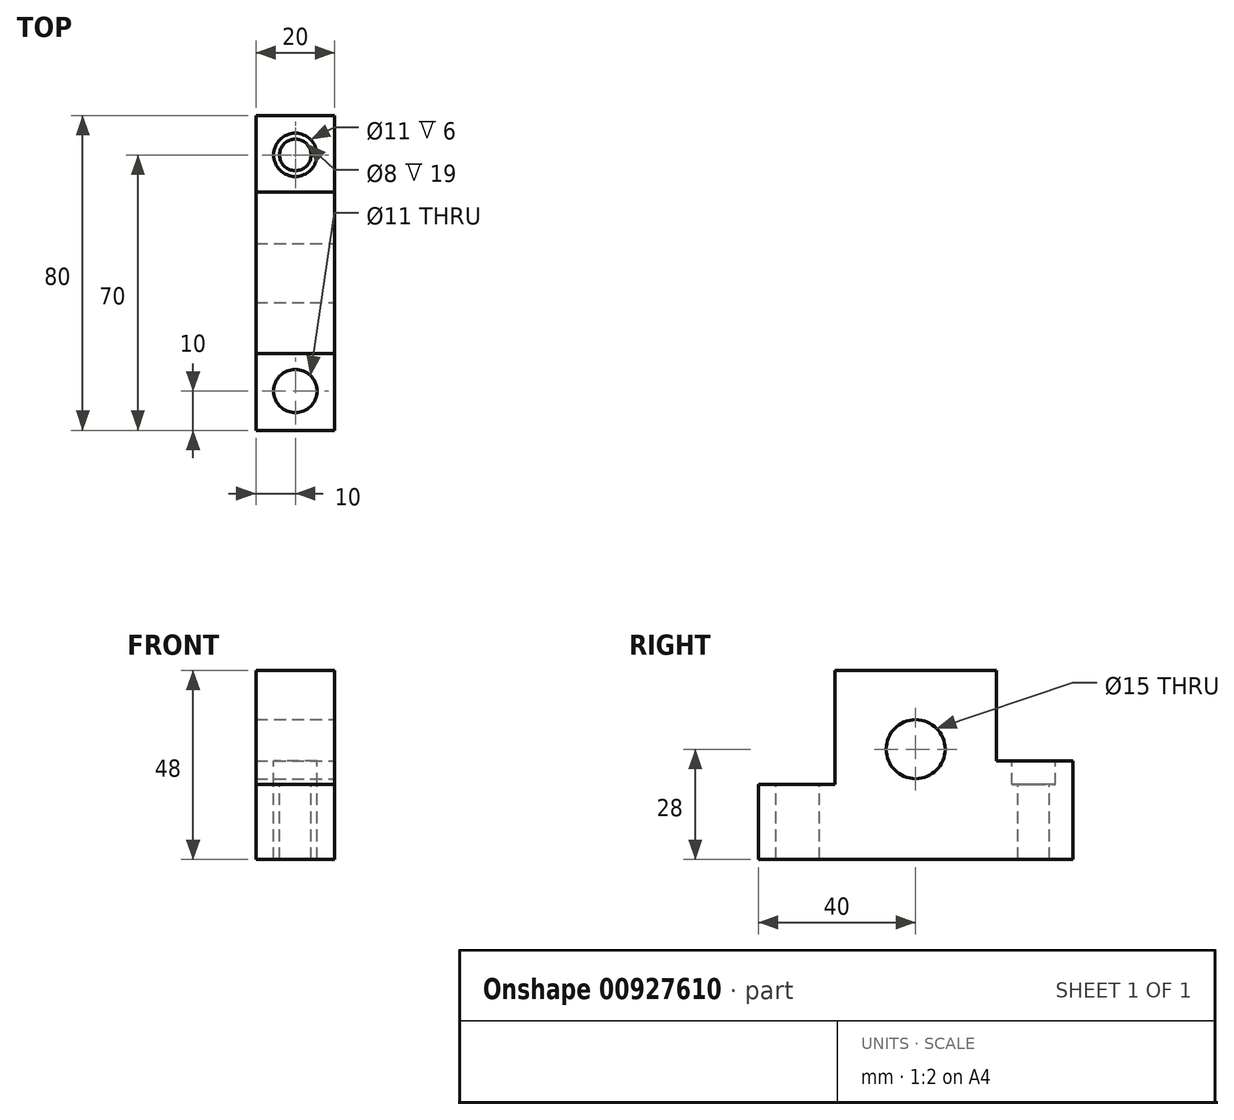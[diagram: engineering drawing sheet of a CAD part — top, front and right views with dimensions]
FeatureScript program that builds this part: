
annotation { "Feature Type Name" : "Feature", "Feature Type Description" : "" }
export const myFeature = defineFeature(function(context is Context, id is Id, definition is map)
    precondition{}
    {
        {
            var Q0;
            Q0=qCreatedBy(makeId("Right.planeOp"),FACE);
            var sketch = newSketch(context, id + "F0", { "sketchPlane" : qUnion([Q0])});
            skLineSegment(sketch, "E0.bottom", {"start": v(40, 24) * mm, "end": v(-40, 24) * mm});
            skLineSegment(sketch, "E0.top", {"start": v(40, -24) * mm, "end": v(-40, -24) * mm});
            skLineSegment(sketch, "E0.left", {"start": v(40, 24) * mm, "end": v(40, -24) * mm});
            skLineSegment(sketch, "E0.right", {"start": v(-40, 24) * mm, "end": v(-40, -24) * mm});
            skPoint(sketch, "E0.middle", {"position": v(0, 0) * mm});
            skSolve(sketch);
        }
        {
            var Q0;
            Q0 = qSketchRegion(id + "F0", true);
            extrude(context, id + "F1", {"entities" : qUnion([Q0]), "depth" : 20 * mm, "offsetDistance" : 25 * mm});
        }
        {
            var Q0;
            Q0=makeQuery(id+"F1.opExtrude","CAP_FACE",FACE,{"disambiguationData":[OSD([sQuery(id+"F0.wireOp",EDGE,"E0.bottom"),sQuery(id+"F0.wireOp",EDGE,"E0.top"),sQuery(id+"F0.wireOp",EDGE,"E0.left"),sQuery(id+"F0.wireOp",EDGE,"E0.right")])],"isStart":false});
            var sketch = newSketch(context, id + "F2", { "sketchPlane" : qUnion([Q0])});
            skLineSegment(sketch, "E1", {"start": v(-74.26, 4) * mm, "end": v(75.01, 4) * mm, "construction": true});
            skCircle(sketch, "E2", {"center": v(0, 4) * mm, "radius": 7.5 * mm});
            skSolve(sketch);
        }
        {
            var Q0;
            Q0=makeQuery(id+"F2.imprint","IMPRINT",FACE,{"disambiguationData":[TD([[makeQuery(id+"F2.imprint","IMPRINT",EDGE,{"derivedFrom":sQuery(id+"F2.wireOp",EDGE,"E2")}),1.0]])]});
            extrude(context, id + "F3", {"entities" : qUnion([Q0]), "operationType" : NewBodyOperationType.REMOVE, "endBound" : BoundingType.THROUGH_ALL, "oppositeDirection" : true, "depth" : 25 * mm, "offsetDistance" : 25 * mm});
        }
        {
            var Q0;
            Q0=makeQuery(id+"F1.opExtrude","CAP_FACE",FACE,{"disambiguationData":[OSD([sQuery(id+"F0.wireOp",EDGE,"E0.bottom"),sQuery(id+"F0.wireOp",EDGE,"E0.top"),sQuery(id+"F0.wireOp",EDGE,"E0.left"),sQuery(id+"F0.wireOp",EDGE,"E0.right")])],"isStart":false});
            var sketch = newSketch(context, id + "F4", { "sketchPlane" : qUnion([Q0])});
            skLineSegment(sketch, "E3", {"start": v(20.5, 56.94) * mm, "end": v(20.5, 1) * mm});
            skLineSegment(sketch, "E4", {"start": v(20.5, 1) * mm, "end": v(58.1, 1) * mm});
            skLineSegment(sketch, "E5.MirrorCS", {"start": v(-20.5, 56.94) * mm, "end": v(-20.5, 1) * mm});
            skLineSegment(sketch, "E6.MirrorCS", {"start": v(-20.5, 1) * mm, "end": v(-58.1, 1) * mm});
            skSolve(sketch);
        }
        {
            var Q0;
            {var subQ0=sQuery(id+"F4.wireOp",EDGE,"E6.MirrorCS");var subQ1=sQuery(id+"F4.wireOp",EDGE,"E5.MirrorCS");var subQ2=makeQuery(id+"F4.imprint","INTERSECT",VERTEX,{"derivedFrom":[subQ1,subQ0]});Q0=makeQuery(id+"F4.imprint","IMPRINT",FACE,{"disambiguationData":[TD([[makeQuery(id+"F4.imprint","IMPRINT",EDGE,{"disambiguationData":[TD([[subQ2,1.0]])],"derivedFrom":subQ1}),-1.0]])]});}
            var Q1;
            {var subQ0=sQuery(id+"F4.wireOp",EDGE,"E4");var subQ1=sQuery(id+"F4.wireOp",EDGE,"E3");var subQ2=makeQuery(id+"F4.imprint","INTERSECT",VERTEX,{"derivedFrom":[subQ1,subQ0]});Q1=makeQuery(id+"F4.imprint","IMPRINT",FACE,{"disambiguationData":[TD([[makeQuery(id+"F4.imprint","IMPRINT",EDGE,{"disambiguationData":[TD([[subQ2,1.0]])],"derivedFrom":subQ1}),1.0]])]});}
            extrude(context, id + "F5", {"entities" : qUnion([Q0, Q1]), "operationType" : NewBodyOperationType.REMOVE, "endBound" : BoundingType.THROUGH_ALL, "oppositeDirection" : true, "depth" : 25 * mm, "offsetDistance" : 25 * mm});
        }
        {
            var Q0;
            Q0=makeQuery(id+"F5.boolean.opBoolean","COPY",FACE,{"derivedFrom":makeQuery(id+"F5.opExtrude","SWEPT_FACE",FACE,{"disambiguationData":[OSD([sQuery(id+"F4.wireOp",EDGE,"E6.MirrorCS")])]})});
            var sketch = newSketch(context, id + "F6", { "sketchPlane" : qUnion([Q0])});
            skLineSegment(sketch, "E7", {"start": v(10, 66.63) * mm, "end": v(10, -85.18) * mm, "construction": true});
            skCircle(sketch, "E8", {"center": v(10, 30) * mm, "radius": 5.5 * mm});
            skCircle(sketch, "E9.MirrorC", {"center": v(10, -30) * mm, "radius": 5.5 * mm});
            skCircle(sketch, "E10", {"center": v(10, 30) * mm, "radius": 4 * mm});
            skCircle(sketch, "E11.MirrorC", {"center": v(10, -30) * mm, "radius": 4 * mm});
            skSolve(sketch);
        }
        {
            var Q0;
            Q0=makeQuery(id+"F6.imprint","IMPRINT",FACE,{"disambiguationData":[TD([[makeQuery(id+"F6.imprint","IMPRINT",EDGE,{"derivedFrom":sQuery(id+"F6.wireOp",EDGE,"E8")}),1.0]])]});
            var Q1;
            Q1=makeQuery(id+"F6.imprint","IMPRINT",FACE,{"disambiguationData":[TD([[makeQuery(id+"F6.imprint","IMPRINT",EDGE,{"derivedFrom":sQuery(id+"F6.wireOp",EDGE,"E9.MirrorC")}),-1.0]])]});
            extrude(context, id + "F7", {"entities" : qUnion([Q0, Q1]), "operationType" : NewBodyOperationType.REMOVE, "oppositeDirection" : true, "depth" : 6 * mm, "offsetDistance" : 25 * mm});
        }
        {
            var Q0;
            Q0=makeQuery(id+"F7.boolean.opBoolean","SPLIT",FACE,{"disambiguationData":[TD([makeQuery(id+"F7.opExtrude","SWEPT_FACE",FACE,{"disambiguationData":[OSD([sQuery(id+"F6.wireOp",EDGE,"E10")])]})])],"derivedFrom":makeQuery(id+"F5.boolean.opBoolean","COPY",FACE,{"derivedFrom":makeQuery(id+"F5.opExtrude","SWEPT_FACE",FACE,{"disambiguationData":[OSD([sQuery(id+"F4.wireOp",EDGE,"E4")])]})})});
            var Q1;
            Q1=makeQuery(id+"F7.boolean.opBoolean","SPLIT",FACE,{"disambiguationData":[TD([makeQuery(id+"F7.opExtrude","SWEPT_FACE",FACE,{"disambiguationData":[OSD([sQuery(id+"F6.wireOp",EDGE,"E11.MirrorC")])]})])],"derivedFrom":makeQuery(id+"F5.boolean.opBoolean","COPY",FACE,{"derivedFrom":makeQuery(id+"F5.opExtrude","SWEPT_FACE",FACE,{"disambiguationData":[OSD([sQuery(id+"F4.wireOp",EDGE,"E6.MirrorCS")])]})})});
            extrude(context, id + "F8", {"entities" : qUnion([Q0, Q1]), "operationType" : NewBodyOperationType.REMOVE, "endBound" : BoundingType.THROUGH_ALL, "oppositeDirection" : true, "depth" : 25 * mm, "offsetDistance" : 25 * mm});
        }
    });
